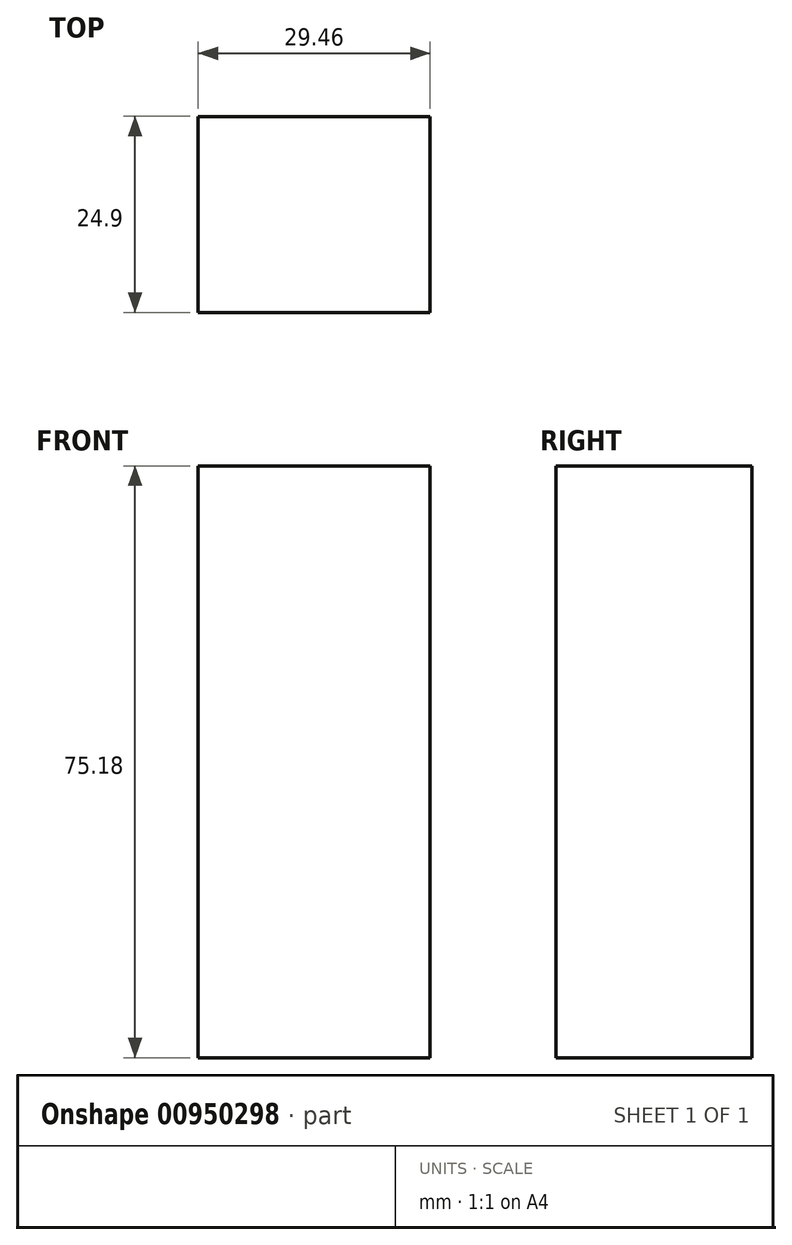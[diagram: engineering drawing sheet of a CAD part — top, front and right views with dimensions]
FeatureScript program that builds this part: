
annotation { "Feature Type Name" : "Feature", "Feature Type Description" : "" }
export const myFeature = defineFeature(function(context is Context, id is Id, definition is map)
    precondition{}
    {
        {
            var Q0;
            Q0=qCreatedBy(makeId("Top.planeOp"),FACE);
            var sketch = newSketch(context, id + "F0", { "sketchPlane" : qUnion([Q0])});
            skLineSegment(sketch, "E0.bottom", {"start": v(14.73, 12.45) * mm, "end": v(-14.73, 12.45) * mm});
            skLineSegment(sketch, "E0.top", {"start": v(14.73, -12.45) * mm, "end": v(-14.73, -12.45) * mm});
            skLineSegment(sketch, "E0.left", {"start": v(14.73, 12.45) * mm, "end": v(14.73, -12.45) * mm});
            skLineSegment(sketch, "E0.right", {"start": v(-14.73, 12.45) * mm, "end": v(-14.73, -12.45) * mm});
            skPoint(sketch, "E0.middle", {"position": v(0, 0) * mm});
            skSolve(sketch);
        }
        {
            var Q0;
            Q0=makeQuery(id+"F0.imprint","IMPRINT",FACE,{"disambiguationData":[TD([[makeQuery(id+"F0.imprint","IMPRINT",EDGE,{"derivedFrom":sQuery(id+"F0.wireOp",EDGE,"E0.bottom")}),1.0]])]});
            extrude(context, id + "F1", {"entities" : qUnion([Q0]), "oppositeDirection" : true, "depth" : 75.18 * mm, "offsetDistance" : 25.4 * mm});
        }
    });
